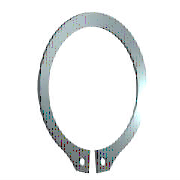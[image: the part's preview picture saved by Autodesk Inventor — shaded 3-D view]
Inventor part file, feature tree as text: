
AUTODESK INVENTOR PART (.ipt)
format: ipt  version: 2011 (Build 150229000, 229)  size: 141,312 bytes
history: native  units: mm (DEFAULTED — no unit token found)
features: sketch x2
ambient origin geometry x8: Origin, YZ Plane, XZ Plane, XY Plane, X Axis, Y Axis, Z Axis, Center Point
feature tree (2):
  sketch  "Sketch2"  dims[d0=0.0mm]
  sketch  "Sketch3"  dims[d2=1.9mm d4=0.55mm d6=2.2mm d8=1.65mm d10=3.3mm d12=0.44mm d14=0.3mm d15=0.466667mm d16=0.6mm d17=0.0mm d18=1.1mm d20=0.99mm d22=0.99mm d24=1.0mm d26=0.13mm d27=0.0mm d28=6.6mm d32=1.4mm d34=3.1mm d35=1.033333mm d36=1.2mm d37=1.55mm d47=3.313333mm d48=2.16mm d49=0.62mm d51=0.0mm d52=0.0mm d53=0.0mm d54=0.0mm]
